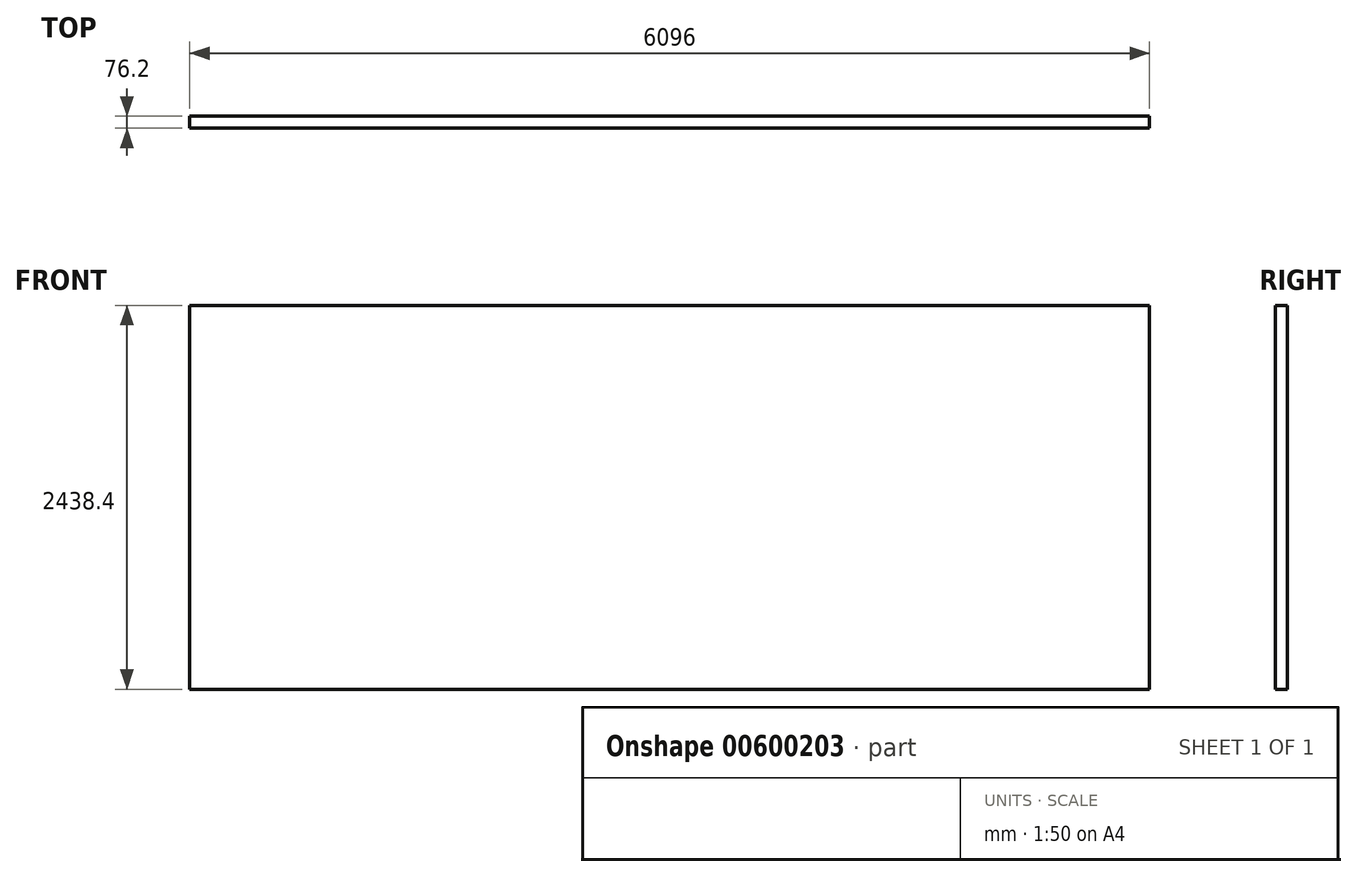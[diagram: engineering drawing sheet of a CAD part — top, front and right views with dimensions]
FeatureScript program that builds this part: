
annotation { "Feature Type Name" : "Feature", "Feature Type Description" : "" }
export const myFeature = defineFeature(function(context is Context, id is Id, definition is map)
    precondition{}
    {
        {
            var Q0;
            Q0=qCreatedBy(makeId("Front.planeOp"),FACE);
            var sketch = newSketch(context, id + "F0", { "sketchPlane" : qUnion([Q0])});
            skLineSegment(sketch, "E0.bottom", {"start": v(-2709.82, 2435.42) * mm, "end": v(3386.18, 2435.42) * mm});
            skLineSegment(sketch, "E0.top", {"start": v(-2709.82, -2.98) * mm, "end": v(3386.18, -2.98) * mm});
            skLineSegment(sketch, "E0.left", {"start": v(-2709.82, 2435.42) * mm, "end": v(-2709.82, -2.98) * mm});
            skLineSegment(sketch, "E0.right", {"start": v(3386.18, 2435.42) * mm, "end": v(3386.18, -2.98) * mm});
            skSolve(sketch);
        }
        {
            var Q0;
            Q0=makeQuery(id+"F0.imprint","IMPRINT",FACE,{"disambiguationData":[TD([[makeQuery(id+"F0.imprint","IMPRINT",EDGE,{"derivedFrom":sQuery(id+"F0.wireOp",EDGE,"E0.bottom")}),-1.0]])]});
            extrude(context, id + "F1", {"entities" : qUnion([Q0]), "depth" : 76.2 * mm, "offsetDistance" : 30.48 * mm});
        }
    });
